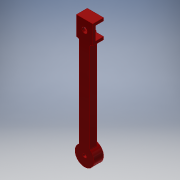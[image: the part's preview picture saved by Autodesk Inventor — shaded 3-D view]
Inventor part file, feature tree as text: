
AUTODESK INVENTOR PART (.ipt)
format: ipt  version: 2019 (Build 230136000, 136)  size: 181,248 bytes
history: native  units: mm
features: extrude x6, sketch x6, other x4, fillet x3, reference x2
ambient origin geometry x8: Origin, YZ Plane, XZ Plane, XY Plane, X Axis, Y Axis, Z Axis, Center Point
bodies: Solid1 (feature_tree)
feature tree (21):
  extrude  "Extrusion1"  Depth=8.0mm
  extrude  "Extrusion2"  Depth=8.0mm
  extrude  "Extrusion3"  Depth=80.0mm
  extrude  "Extrusion4"  Depth=1.0mm
  fillet  "Fillet1"  Radius=4.1mm
  extrude  "Extrusion5"  Depth=3.0mm
  fillet  "Fillet2"  Radius=2.5mm
  fillet  "Fillet3"  Radius=3.0mm
  extrude  "Extrusion6"  Depth=2.0mm
  sketch  "Sketch1"  dims[d0=8.0mm d1=14.0mm]
  sketch  "Sketch2"  dims[d2=8.0mm d3=12.0mm]
  sketch  "Sketch3"  dims[d4=14.0mm d6=80.0mm]
  sketch  "Sketch4"  dims[d7=3.0mm d8=1.0mm d9=4.1mm]
  sketch  "Sketch5"  dims[d10=8.0mm d11=0.0mm d12=8.1mm d13=2.5mm d14=0.0mm d15=3.0mm d16=0.0mm]
  reference  "Reference1"
  reference  "Reference2"
  sketch  "Sketch6"  dims[d17=2.0mm d18=2.0mm d19=6.0mm d20=0.0mm d21=1.0mm d22=1.0mm d23=2.0mm d24=0.0mm d25=0.1mm d26=0.4mm d27=1.0mm d28=0.0mm]
  parser-record x1  (decoder bookkeeping rows leaked as tree rows — omitted from the tree; the rows remain in map.json)
  other  "Kinematics.iam"
  other  "Motor-GM15BY:2"
  other  "Motor-Body:1"
note: 1 file-system path scrubbed to <path> (originals preserved in map.json)
